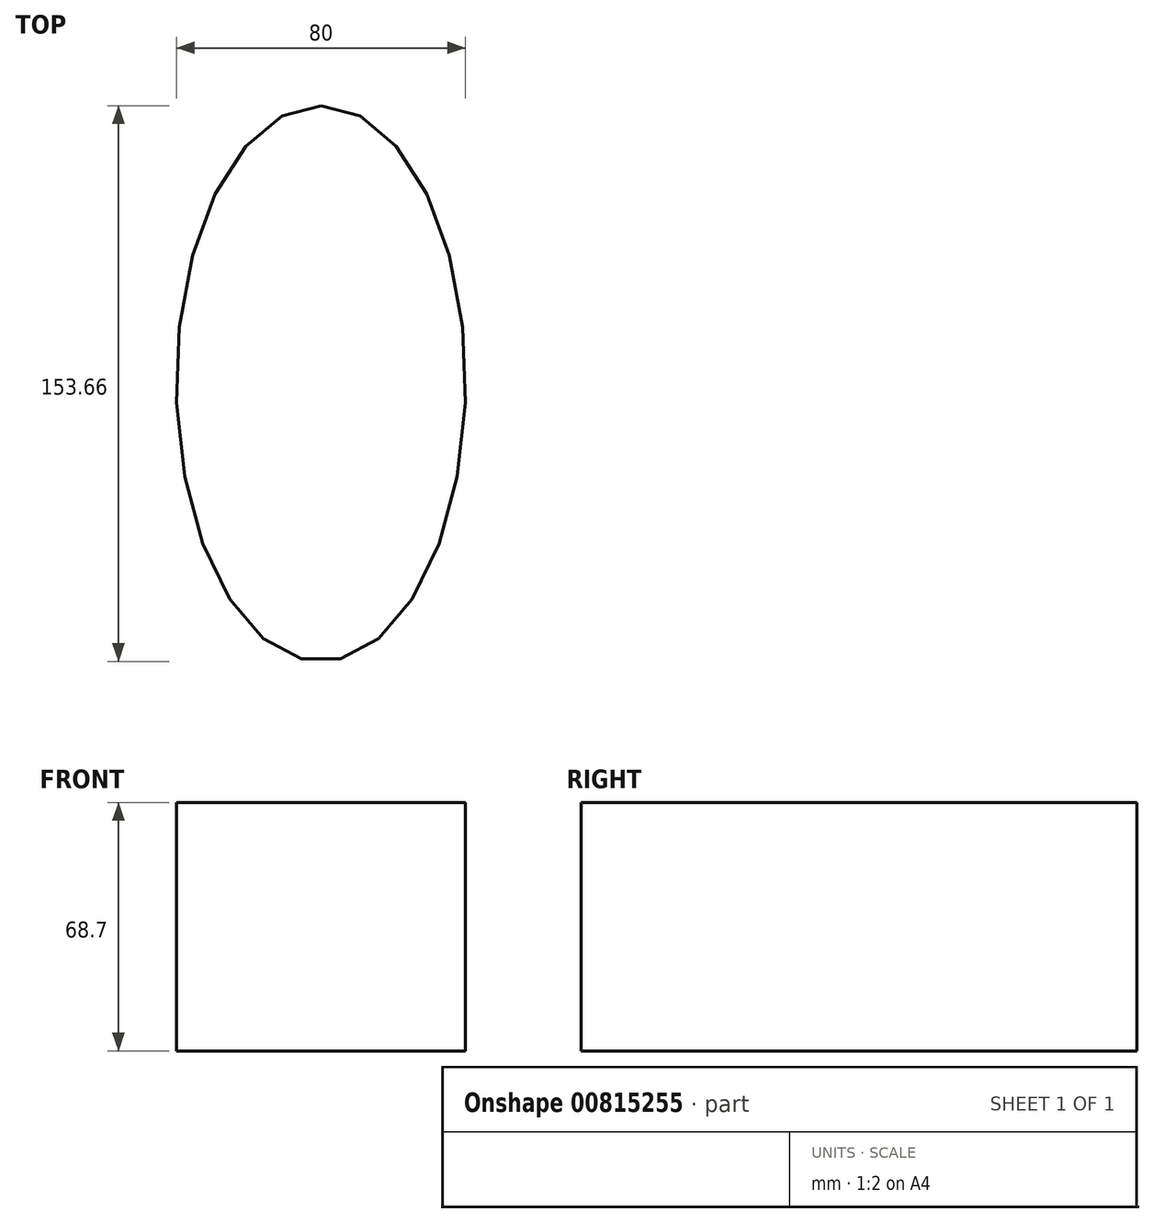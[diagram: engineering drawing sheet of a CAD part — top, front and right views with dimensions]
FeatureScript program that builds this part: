
annotation { "Feature Type Name" : "Feature", "Feature Type Description" : "" }
export const myFeature = defineFeature(function(context is Context, id is Id, definition is map)
    precondition{}
    {
        {
            var Q0;
            Q0=qCreatedBy(makeId("Top.planeOp"),FACE);
            var sketch = newSketch(context, id + "F0", { "sketchPlane" : qUnion([Q0])});
            skEllipse(sketch, "E0", {"center": v(0, 0) * mm, "majorRadius": 76.83 * mm, "minorRadius": 40 * mm, "majorAxis": v(0, 1)});
            skSolve(sketch);
        }
        {
            var Q0;
            Q0=makeQuery(id+"F0.imprint","IMPRINT",FACE,{"disambiguationData":[TD([[makeQuery(id+"F0.imprint","IMPRINT",EDGE,{"derivedFrom":sQuery(id+"F0.wireOp",EDGE,"E0")}),1.0]])]});
            extrude(context, id + "F1", {"entities" : qUnion([Q0]), "oppositeDirection" : true, "depth" : 68.7 * mm, "offsetDistance" : 25 * mm});
        }
    });
